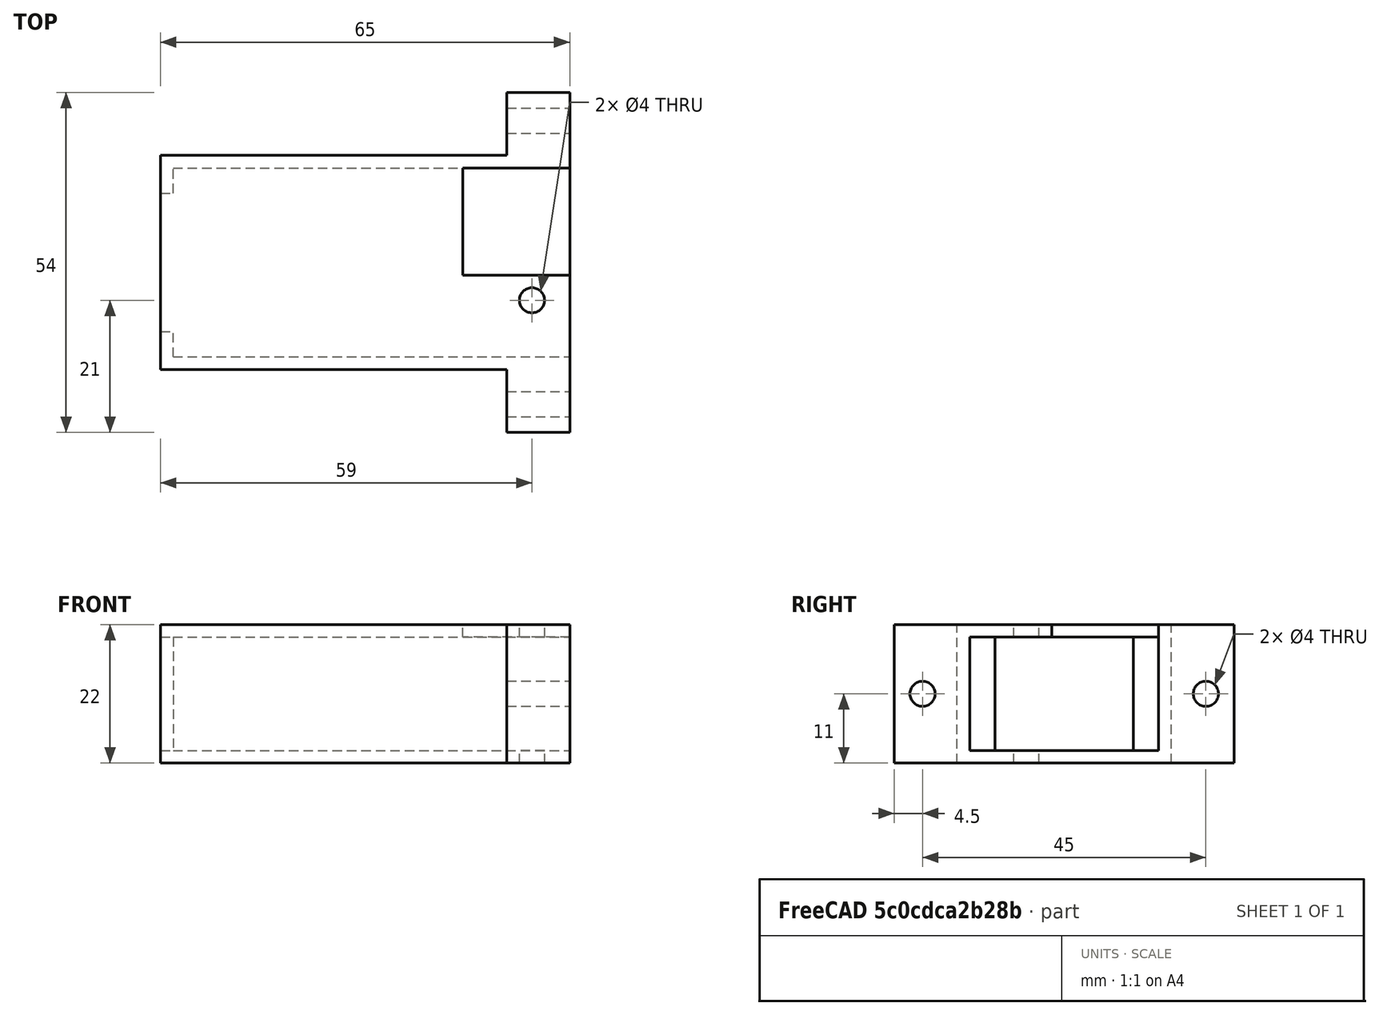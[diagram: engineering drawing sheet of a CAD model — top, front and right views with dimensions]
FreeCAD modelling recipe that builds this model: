
FCSTD DOCUMENT  (FreeCAD 0.19R24276 (Git))
Label: EthernetCover
License: All rights reserved
LicenseURL: http://en.wikipedia.org/wiki/All_rights_reserved
objects: Part::Box×6, Part::MultiFuse×4, Part::Cylinder×3, Part::Cut×2, Spreadsheet::Sheet×1
note: 15 computed .brp shape members not serialized (recipe doc carries the construction recipe); baked Part::Feature solids carry a one-line shape summary decoded from their .brp

FEATURE [Part::Box] Box  label="Body"
  AttacherType = Attacher::AttachEngine3D
  Height = 22
  Length = 65
  Width = 54
  expr: Width = <<dims>>.BodyWidth
  expr: Height = <<dims>>.BodyHeight
  expr: Length = <<dims>>.BodyLength
  expr: .Placement.Base.x = 0mm
FEATURE [Spreadsheet::Sheet] Spreadsheet  label="dims"
  cells = A2=BodyWidth; B2(BodyWidth)==54mm; A3=BodyHeight; B3(BodyHeight)==22mm; A4=BodyLength; B4(BodyLength)==65mm; A5=CutDepth; B5(CutDepth)==10mm; A6=CutLength; B6(CutLength)==10mm; A7=Hole Diameter; B7(HoleDiameter)==4mm; A8=Hole Separation; B8(HoleSeparation)==45mm; A9=Wall Width; B9(WallWidth)==2mm; A10=Back Stop; B10(BackStop)==2mm; A11=Exterior Lip; B11(ExteriorLip)==0mm; A12=Exterior Lip Width; B12(ExteriorLipWidth)==4mm; A13=Capture Screw Diameter; B13(CaptureScrewDiameter)==4mm; A14=Capture Screw Set Back; B14(CaptureScrewSetBack)==57mm; A15=Capture Screw Offset; B15(CaptureScrewOffset)==-6mm; A16=Notch Depth; B16(NotchDepth)==17mm
FEATURE [Part::Box] Box001  label="LeftCut"
  AttacherType = Attacher::AttachEngine3D
  Height = 22
  Length = 55
  Width = 10
  expr: Length = <<dims>>.BodyLength - <<dims>>.CutLength
  expr: Height = <<dims>>.BodyHeight
  expr: Width = <<dims>>.CutDepth
FEATURE [Part::Box] Box002  label="RightCut"
  AttacherType = Attacher::AttachEngine3D
  Height = 22
  Length = 55
  Placement = pos=(0,44,0) rot=(0,0,1;0rad)
  Width = 10
  expr: Length = <<dims>>.BodyLength - <<dims>>.CutLength
  expr: Width = <<dims>>.CutDepth
  expr: Height = <<dims>>.BodyHeight
  expr: .Placement.Base.y = <<dims>>.BodyWidth - <<dims>>.CutDepth
FEATURE [Part::MultiFuse] Fusion  label="SideCuts"
  Shapes = -> [Box001,Box002]
FEATURE [Part::Cylinder] Cylinder  label="LeftHole"
  Angle = 360
  AttacherType = Attacher::AttachEngine3D
  Height = 65
  Placement = pos=(0,4.5,11) rot=(0,1,0;1.5708rad)
  Radius = 2
  expr: Height = <<dims>>.BodyLength
  expr: Radius = <<dims>>.HoleDiameter / 2
  expr: .Placement.Base.z = <<dims>>.BodyHeight / 2
  expr: .Placement.Base.y = (<<dims>>.BodyWidth - <<dims>>.HoleSeparation) / 2
FEATURE [Part::Cylinder] Cylinder001  label="RightHole"
  Angle = 360
  AttacherType = Attacher::AttachEngine3D
  Height = 65
  Placement = pos=(0,49.5,11) rot=(0,1,0;1.5708rad)
  Radius = 2
  expr: .Placement.Base.y = (<<dims>>.BodyWidth + <<dims>>.HoleSeparation) / 2
  expr: .Placement.Base.z = <<dims>>.BodyHeight / 2
  expr: Radius = <<dims>>.HoleDiameter / 2
  expr: Height = <<dims>>.BodyLength
FEATURE [Part::MultiFuse] Fusion001  label="MountingHoles"
  Shapes = -> [Cylinder,Cylinder001]
FEATURE [Part::MultiFuse] Fusion002  label="CutoutsAndMounting"
  Shapes = -> [Fusion,Fusion001]
FEATURE [Part::Cut] Cut  label="BodyWithMounting"
  Base = -> Box
  Tool = -> Fusion002
FEATURE [Part::Box] Box003  label="CavityCutOut"
  AttacherType = Attacher::AttachEngine3D
  Height = 18
  Length = 63
  Placement = pos=(2,12,2) rot=(0,0,1;0rad)
  Width = 30
  expr: Width = <<dims>>.BodyWidth - 2 * <<dims>>.CutDepth - 2 * <<dims>>.WallWidth
  expr: Height = <<dims>>.BodyHeight - 2 * <<dims>>.WallWidth
  expr: Length = <<dims>>.BodyLength - <<dims>>.BackStop
  expr: .Placement.Base.z = <<dims>>.BackStop
  expr: .Placement.Base.y = <<dims>>.CutDepth + <<dims>>.WallWidth
  expr: .Placement.Base.x = <<dims>>.WallWidth
FEATURE [Part::Box] Box004  label="CavityCutWall"
  AttacherType = Attacher::AttachEngine3D
  Height = 18
  Length = 65
  Placement = pos=(0,16,2) rot=(0,0,1;0rad)
  Width = 22
  expr: .Placement.Base.x = <<dims>>.WallWidth * 0
  expr: .Placement.Base.y = <<dims>>.CutDepth + <<dims>>.WallWidth + <<dims>>.ExteriorLipWidth
  expr: .Placement.Base.z = <<dims>>.BackStop + <<dims>>.ExteriorLip
  expr: Length = <<dims>>.BodyLength
  expr: Height = <<dims>>.BodyHeight - 2 * <<dims>>.WallWidth - 2 * <<dims>>.ExteriorLip
  expr: Width = <<dims>>.BodyWidth - 2 * <<dims>>.CutDepth - 2 * <<dims>>.WallWidth - 2 * <<dims>>.ExteriorLipWidth
FEATURE [Part::Cylinder] Cylinder002  label="CaptureScrewHole"
  Angle = 360
  AttacherType = Attacher::AttachEngine3D
  Height = 22
  Placement = pos=(59,21,0) rot=(0,0,1;0rad)
  Radius = 2
  expr: Radius = <<dims>>.CaptureScrewDiameter / 2
  expr: Height = <<dims>>.BodyHeight
  expr: .Placement.Base.x = <<dims>>.CaptureScrewSetBack + <<dims>>.BackStop
  expr: .Placement.Base.y = <<dims>>.BodyWidth / 2 + <<dims>>.CaptureScrewOffset
FEATURE [Part::Box] Box005  label="CutAwayNotch"
  AttacherType = Attacher::AttachEngine3D
  Height = 20
  Length = 17
  Placement = pos=(48,25,2) rot=(0,0,1;0rad)
  Width = 17
  expr: .Placement.Base.z = <<dims>>.WallWidth
  expr: Width = <<dims>>.BodyWidth / 2 - <<dims>>.CutDepth
  expr: .Placement.Base.x = <<dims>>.BodyLength - <<dims>>.NotchDepth
  expr: Length = <<dims>>.NotchDepth
  expr: .Placement.Base.y = <<dims>>.BodyWidth / 2 + <<dims>>.CaptureScrewOffset + 2 * <<dims>>.WallWidth
  expr: Height = <<dims>>.BodyHeight - <<dims>>.WallWidth
FEATURE [Part::MultiFuse] Fusion003  label="InteriorCut"
  Shapes = -> [Box004,Box003,Cylinder002,Box005]
FEATURE [Part::Cut] Cut001  label="EthernetMount"
  Base = -> Cut
  Tool = -> Fusion003
